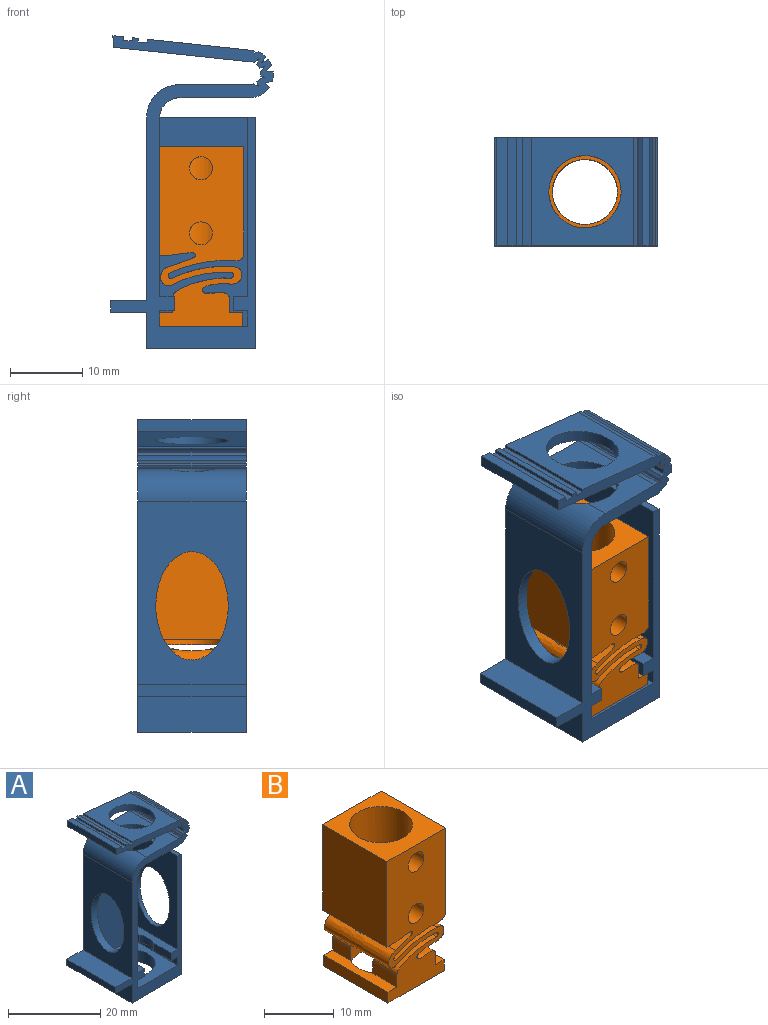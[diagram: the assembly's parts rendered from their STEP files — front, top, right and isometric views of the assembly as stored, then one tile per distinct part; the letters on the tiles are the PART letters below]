
ASSEMBLY  parts=2 mates=1
PART A: 72 faces, bbox 22.5x15x43.3 mm
  f0: cylinder r=4.46mm len=15mm, axis (0,1,0), area 93.9mm2, adj f9,f12,f14,f58,f70
  f1: cylinder r=2.66mm len=15mm, axis (0,1,0), area 50.9mm2, adj f6,f12,f14,f19,f59,f70
  f2: plane 5.32x2mm, normal (-1,0,0), area 10.6mm2, adj f14,f62,f63,f69
  f3: plane 4.32x2mm, normal (-1,0,0), area 8.6mm2, adj f7,f62,f63,f69
  f4: plane 4.14x2mm, normal (1,0,0), area 8.3mm2, adj f14,f64,f65,f68
  f5: plane 3.14x2mm, normal (1,0,0), area 6.3mm2, adj f7,f64,f65,f68
  f6: plane 24.8x14mm, normal (1,0,0), area 229.2mm2, adj f1,f7,f14,f64,f66
  f7: plane 29x12.2mm, normal (0,-1,0), area 345.8mm2, adj f3,f5,f6,f8,f10,f17,f18,f19
  f8: plane 24.8x14mm, normal (-1,0,0), area 229.2mm2, adj f7,f14,f19,f62,f67
  f9: plane 25.4x15mm, normal (-1,0,0), area 263mm2, adj f0,f12,f14,f22,f66
  f10: plane 14x12.2mm, normal (0,0,1), area 92.3mm2, adj f7,f14,f15,f17,f18
  f11: plane 32x15mm, normal (1,0,0), area 362mm2, adj f12,f14,f16,f19,f67
  f12: plane 43.26x22.52mm, normal (0,1,0), area 556.2mm2, adj f0,f1,f9,f11,f13,f16,f19,f20
  f13: plane 15x5mm, normal (-1,0,0), area 75mm2, adj f12,f14,f16,f21
  f14: plane 43.26x22.52mm, normal (0,-1,0), area 210.4mm2, adj f0,f1,f2,f4,f6,f8,f9,f10
  f15: cylinder r=5mm len=10mm, axis (0,0,-1), area 94.2mm2, adj f10,f16
  f16: plane 15x15mm, normal (0,0,-1), area 146.5mm2, adj f11,f12,f13,f14,f15
  f17: plane 14x2.2mm, normal (1,0,0), area 30.8mm2, adj f7,f10,f14,f65
  f18: plane 14x2.2mm, normal (-1,0,0), area 30.8mm2, adj f7,f10,f14,f63
  f19: plane 15x13.2mm, normal (0,0,1), area 27.2mm2, adj f1,f7,f8,f11,f12,f14
  f20: plane 15x1.6mm, normal (-1,0,0), area 24mm2, adj f12,f14,f21,f22
  f21: plane 15x5mm, normal (0,0,-1), area 75mm2, adj f12,f13,f14,f20
  f22: plane 15x5mm, normal (0,0,1), area 75mm2, adj f9,f12,f14,f20
  f23: plane 15x0.9mm, normal (0.24,0,-0.97), area 14mm2, adj f12,f14,f24,f61
  f24: cylinder r=3.3mm len=15mm, axis (0,1,0), area 20.2mm2, adj f12,f14,f23,f25
  f25: plane 15x0.89mm, normal (0.14,0,0.99), area 13.5mm2, adj f12,f14,f24,f26
  f26: plane 15x0.7mm, normal (0.71,0,-0.71), area 14.9mm2, adj f12,f14,f25,f27
  f27: cylinder r=3.3mm len=15mm, axis (0,1,0), area 15.1mm2, adj f12,f14,f26,f28
  f28: plane 15x0.94mm, normal (-0.44,0,0.9), area 15.6mm2, adj f12,f14,f27,f29
  f29: plane 15x0.85mm, normal (0.83,0,-0.56), area 15.4mm2, adj f12,f14,f28,f30
  f30: cylinder r=3.3mm len=15mm, axis (0,1,0), area 19.2mm2, adj f12,f14,f29,f31
  f31: plane 15x0.43mm, normal (-0.47,0,0.88), area 7.2mm2, adj f12,f14,f30,f32
  f32: plane 15x0.4mm, normal (0.87,0,0.5), area 7mm2, adj f12,f14,f31,f33
  f33: cylinder r=3.3mm len=15mm, axis (0,1,0), area 7.8mm2, adj f12,f14,f32,f34
  f34: plane 15x14.17mm, normal (0.11,0,0.99), area 134.8mm2, adj f12,f14,f33,f35,f71
  f35: plane 15x0.41mm, normal (-1,0,0), area 6.1mm2, adj f12,f14,f34,f36
  f36: plane 15x1.2mm, normal (0,0,1), area 18mm2, adj f12,f14,f35,f37
  f37: plane 15x0.53mm, normal (1,0,0), area 8mm2, adj f12,f14,f36,f38
  f38: plane 15x0.85mm, normal (0.11,0,0.99), area 12.8mm2, adj f12,f14,f37,f39
  f39: plane 15x0.45mm, normal (-1,0,0), area 6.7mm2, adj f12,f14,f38,f40
  f40: plane 15x1.2mm, normal (0,0,1), area 18mm2, adj f12,f14,f39,f41
  f41: plane 15x0.58mm, normal (1,0,0), area 8.6mm2, adj f12,f14,f40,f42
  f42: plane 15x1.47mm, normal (0.11,0,0.99), area 22.2mm2, adj f12,f14,f41,f43
  f43: plane 15x1.61mm, normal (-1,0,-0.01), area 24.1mm2, adj f12,f14,f42,f44
  f44: plane 18.79x15mm, normal (-0.11,0,-0.99), area 204.4mm2, adj f12,f14,f43,f45,f71
  f45: cylinder r=1.6mm len=15mm, axis (0,1,0), area 11.5mm2, adj f12,f14,f44,f46
  f46: plane 15x0.59mm, normal (0.71,0,-0.7), area 12.4mm2, adj f12,f14,f45,f47
  f47: plane 15x0.81mm, normal (-0.96,0,0.27), area 12.6mm2, adj f12,f14,f46,f48
  f48: cylinder r=1.6mm len=15mm, axis (0,1,0), area 10mm2, adj f12,f14,f47,f49
  f49: plane 15x0.68mm, normal (0.37,0,-0.93), area 11mm2, adj f12,f14,f48,f50
  f50: plane 15x0.75mm, normal (-0.81,0,0.58), area 13.8mm2, adj f12,f14,f49,f51
  f51: cylinder r=1.6mm len=15mm, axis (0,1,0), area 9.2mm2, adj f12,f14,f50,f52
  f52: plane 15x0.54mm, normal (-0.28,0,-0.96), area 8.5mm2, adj f12,f14,f51,f53
  f53: plane 15x0.71mm, normal (-0.34,0,0.94), area 11.3mm2, adj f12,f14,f52,f54
  f54: cylinder r=1.6mm len=15mm, axis (0,1,0), area 8.1mm2, adj f12,f14,f53,f55
  f55: plane 15x0.64mm, normal (-0.95,0,-0.31), area 10mm2, adj f12,f14,f54,f56
  f56: plane 15x0.64mm, normal (0.5,0,0.87), area 11mm2, adj f12,f14,f55,f57
  f57: cylinder r=1.6mm len=15mm, axis (0,1,0), area 9.2mm2, adj f12,f14,f56,f58
  f58: plane 15x9.76mm, normal (0,0,1), area 78.7mm2, adj f0,f12,f14,f57,f70
  f59: plane 15x9.76mm, normal (0,0,-1), area 78.7mm2, adj f1,f12,f14,f60,f70
  f60: cylinder r=3.3mm len=15mm, axis (0,1,0), area 48.2mm2, adj f12,f14,f59,f61
  f61: plane 15x0.6mm, normal (0.77,0,0.64), area 11.7mm2, adj f12,f14,f23,f60
  f62: plane 14x2mm, normal (0,0,1), area 26.5mm2, adj f2,f3,f7,f8,f14,f69
  f63: plane 14x2mm, normal (0,0,-1), area 26.5mm2, adj f2,f3,f7,f14,f18,f69
  f64: plane 14x2mm, normal (0,0,1), area 22mm2, adj f4,f5,f6,f7,f14,f68
  f65: plane 14x2mm, normal (0,0,-1), area 22mm2, adj f4,f5,f7,f14,f17,f68
  f66: extruded ~15x10.01mm, area 71.4mm2, adj f6,f9
  f67: extruded ~15x10.01mm, area 39.7mm2, adj f8,f11
  f68: cylinder r=5mm len=6.73mm, axis (0,0,-1), area 14.8mm2, adj f4,f5,f64,f65
  f69: cylinder r=5mm len=4.36mm, axis (0,0,-1), area 9mm2, adj f2,f3,f62,f63
  f70: cylinder r=5mm len=10mm, axis (0,0,-1), area 58.3mm2, adj f0,f1,f58,f59
  f71: cylinder r=5mm len=10mm, axis (0,0,-1), area 50.5mm2, adj f34,f44
PART B: 37 faces, bbox 11.8x13x24.9 mm
  f0: cylinder r=4.5mm len=24.9mm, axis (0,0,1), area 587.4mm2, adj f1,f2,f3,f4,f5,f6,f7,f8
  f1: plane 3.66x2mm, normal (-1,0,0), area 7.3mm2, adj f0,f10,f12,f34
  f2: plane 3.66x2mm, normal (1,0,0), area 7.3mm2, adj f0,f3,f16,f34
  f3: extruded ~4.01x3.91mm, area 18.6mm2, adj f0,f2,f19,f34
  f4: cylinder r=16.42mm len=8.36mm, axis (0,1,0), area 29.2mm2, adj f0,f5,f19,f33
  f5: cylinder r=0.45mm len=7.03mm, axis (0,1,0), area 6.3mm2, adj f0,f4,f6,f33
  f6: cylinder r=17.22mm len=8.47mm, axis (0,1,0), area 29.9mm2, adj f0,f5,f23,f33
  f7: extruded ~4.05x3.33mm, area 16.5mm2, adj f0,f27,f29,f34
  f8: cylinder r=15.62mm len=8.31mm, axis (0,1,0), area 29.1mm2, adj f0,f9,f29,f33
  f9: cylinder r=0.41mm len=6.8mm, axis (0,1,0), area 6.7mm2, adj f0,f8,f32,f33
  f10: extruded ~8.05x4.17mm, area 19.9mm2, adj f0,f1,f31,f34
  f11: plane 4.86x2mm, normal (-1,0,0), area 9.7mm2, adj f0,f12,f32,f33
  f12: plane 13x1.8mm, normal (0,0,1), area 21.6mm2, adj f0,f1,f11,f13,f33,f34
  f13: plane 13x1.9mm, normal (-1,0,0), area 24.7mm2, adj f12,f14,f33,f34
  f14: plane 13x11.4mm, normal (0,0,-1), area 84.6mm2, adj f0,f13,f15,f33,f34
  f15: plane 13x1.9mm, normal (1,0,0), area 24.7mm2, adj f14,f16,f33,f34
  f16: plane 13x1.8mm, normal (0,0,1), area 21.6mm2, adj f0,f2,f15,f17,f33,f34
  f17: plane 4.86x2mm, normal (1,0,0), area 9.7mm2, adj f0,f16,f18,f33
  f18: extruded ~5.21x3.91mm, area 29mm2, adj f0,f17,f19,f33
  f19: extruded ~13x2.4mm, area 55.3mm2, adj f0,f3,f4,f18,f20,f33,f34
  f20: cylinder r=16.42mm len=8.36mm, axis (0,1,0), area 18.9mm2, adj f0,f19,f21,f34
  f21: cylinder r=0.45mm len=5.83mm, axis (0,1,0), area 5.1mm2, adj f0,f20,f22,f34
  f22: cylinder r=17.22mm len=8.47mm, axis (0,1,0), area 19.4mm2, adj f0,f21,f23,f34
  f23: extruded ~13x1.8mm, area 27.7mm2, adj f0,f6,f22,f24,f33,f34
  f24: plane 15x13mm, normal (1,0,0), area 195mm2, adj f23,f25,f33,f34
  f25: plane 13x11.8mm, normal (0,0,1), area 89.8mm2, adj f0,f24,f26,f33,f34
  f26: plane 15x13mm, normal (-1,0,0), area 195mm2, adj f25,f27,f33,f34
  f27: plane 13x1.8mm, normal (0,0,-1), area 22.4mm2, adj f0,f7,f26,f28,f33,f34
  f28: extruded ~5.25x3.33mm, area 25.2mm2, adj f0,f27,f29,f33
  f29: extruded ~13x2.74mm, area 59.1mm2, adj f0,f7,f8,f28,f30,f33,f34
  f30: cylinder r=15.62mm len=8.31mm, axis (0,1,0), area 18.7mm2, adj f0,f29,f31,f34
  f31: cylinder r=0.41mm len=5.6mm, axis (0,1,0), area 5.4mm2, adj f0,f10,f30,f34
  f32: extruded ~8.05x5.37mm, area 30.8mm2, adj f0,f9,f11,f33
  f33: plane 24.9x11.8mm, normal (0,-1,0), area 231.2mm2, adj f4,f5,f6,f8,f9,f11,f12,f13
  f34: plane 24.9x11.8mm, normal (0,1,0), area 247.2mm2, adj f1,f2,f3,f7,f10,f12,f13,f14
  f35: cylinder r=1.6mm len=3.2mm, axis (0,-1,0), area 26.1mm2, adj f0,f33
  f36: cylinder r=1.6mm len=3.2mm, axis (0,-1,0), area 26.1mm2, adj f0,f33
PLACE A t=(-13.93,9.55,-10.18)mm
PLACE B t=(-16.07,15.45,-25.94)mm
MATE fastened B.f0 <-> A.f15  axis (0,0,-1) through (-13.93,9.55,-7.18)mm
